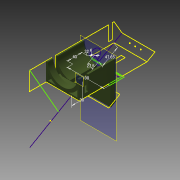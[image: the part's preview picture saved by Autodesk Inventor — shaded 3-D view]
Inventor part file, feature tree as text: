
AUTODESK INVENTOR PART (.ipt)
format: ipt  version: 2013 (Build 170138000, 138)  size: 368,128 bytes
history: native  units: mm
features: sketch x22, extrude x16, other x3, hole x1
ambient origin geometry x8: Origin, YZ Plane, XZ Plane, XY Plane, X Axis, Y Axis, Z Axis, Center Point
feature tree (42):
  other  "ソリッド1"
  extrude  "押し出し1"  Depth=90.0mm
  extrude  "押し出し2"  Depth=50.0mm
  extrude  "押し出し3"  Depth=5.0mm
  extrude  "押し出し4"  Depth=85.0mm
  extrude  "押し出し6"  Depth=5.0mm
  sketch  "スケッチ9"
  hole  "穴1"  [1 undecoded]
  extrude  "押し出し12"  Depth=10.0mm
  sketch  "スケッチ19"
  sketch  "スケッチ20"
  other  "作業平面5"
  extrude  "押し出し13"  Depth=90.0mm
  other  "作業平面6"
  extrude  "押し出し14"  Depth=230.0mm TaperAngle=0.0deg
  extrude  "押し出し15"  Depth=225.0mm TaperAngle=0.0deg
  sketch  "スケッチ24"
  sketch  "スケッチ25"
  extrude  "押し出し16"  Depth=5.0mm TaperAngle=0.0deg
  sketch  "スケッチ27"
  extrude  "押し出し17"  Depth=60.0mm
  extrude  "押し出し18"  Depth=10.0mm
  extrude  "押し出し19"  Depth=140.0mm
  extrude  "押し出し20"  Depth=10.0mm
  extrude  "押し出し21"  Depth=40.0mm
  extrude  "押し出し22"  Depth=90.0mm TaperAngle=0.0deg
  sketch  "スケッチ1"
  sketch  "スケッチ2"
  sketch  "スケッチ3"
  sketch  "スケッチ4"
  sketch  "スケッチ6"
  sketch  "スケッチ11"
  sketch  "スケッチ18"
  sketch  "スケッチ21"
  sketch  "スケッチ22"
  sketch  "スケッチ23"
  sketch  "スケッチ26"
  sketch  "スケッチ28"
  sketch  "スケッチ29"
  sketch  "スケッチ30"
  sketch  "スケッチ31"
  sketch  "スケッチ32"
note: 1 required parameter value undecoded (feature->parameter linkage not recoverable at this tier; creation-order binding heuristic only, values carry confidence <= 0.55)
